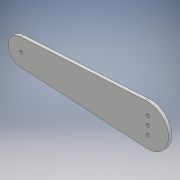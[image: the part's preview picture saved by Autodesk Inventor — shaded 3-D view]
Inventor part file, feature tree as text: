
AUTODESK INVENTOR PART (.ipt)
format: ipt  version: 2018 (Build 220112000, 112)  size: 109,568 bytes
history: native  units: mm
features: other x1, extrude x1, sketch x1
ambient origin geometry x8: Origin, YZ Plane, XZ Plane, XY Plane, X Axis, Y Axis, Z Axis, Center Point
bodies: Body1 (feature_tree)
feature tree (3):
  other  "Sólido1"
  extrude  "Extrusión1"  Depth=3.0mm
  sketch  "Boceto1"  dims[d26=30.0mm d107=3.0mm d113=3.0mm d114=0.0mm]
